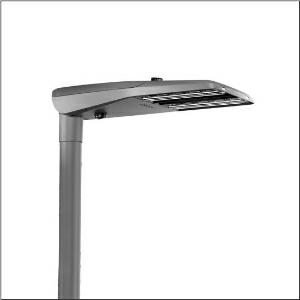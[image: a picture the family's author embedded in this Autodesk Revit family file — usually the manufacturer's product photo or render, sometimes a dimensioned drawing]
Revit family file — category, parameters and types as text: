
# Revit family: streetlight_sl_11_iq_midi___st1_2a_5xc3a21y08me_d9a7
name_source: partatom
category: Lighting Fixtures
units: mm (PartAtom-declared; Revit-internal decimal feet)

## family parameters
Cut with Voids When Loaded = No
Host = Face
Light Source = No
Part Type = Normal
Room Calculation Point = No
Round Connector Dimension = Use Diameter
Shared = No

## types (1)
- --- (1 x LED, 14840 lm, 122.8 W, 2200K)
    Apparent Load = 123 VA
    CIE Flux Codes = 32 70 96 100 100
    Color Rendering = 70
    Color Temperature = 2200K
    Default Elevation = 1800 mm
    Description = Streetlight SL 11 iQ midi, mast luminaire, primary light control with 3 zone facetted reflector, of plastic, silver coated, highly specular, primary optical cover: cover, of PMMA, transparent, light distribution: ST1.2a, light emission: direct distribution, primary light characteristic: asymmetric, installation type: post-top, side-entry, lamps: LED, High Power LED, rated values: 14.840lm | 122,8W | 120,8lm/W (begin service life); end service life: 14.840lm | 130,2W; at 50% lumin. flux: 7.420lm | 56,1W | 132,3lm/W, colour temperature: 2200K, colour rendering: CRI > 70, light colour: 722, light setting 1 begin service life: 100% | 14.840lm | 122,8W | 120,8lm/W | 2.200K, light setting 1 end service life: 130,2W, further light settings possible, control: pre-setting: logarithmic dimming characteristic, Street-Remote, Auto-Match, Temp-Guard, Lumen-Switch, Night-Set, Smart-Wire, Light-Fading, Desk-Remote (wireless, voltage-free reading and setting of iQ features in the workshop via application-optimized NFC function/RFID function), optimised constant luminous flux control (CLO 2.0), with cable H07RN-F 5x 1.5mm², mains connection: 230..240V, AC, 50/60Hz, connection cable pre-assembled, cable length: 12,5m, luminaire housing, of diecast aluminium, powder-coated, Siteco® metallic grey (DB 702S), please order mast flange separately, inclination adjustable without tools: 0°, 5°, 10°, 15° (post-top) | 0°, -5°, -10°, -15° (side-entry), sealing non-destructively replaceable, multi-level sealing system, length: 780mm, width: 376mm, height: 118mm, mast flange for spigot size: 42mm (side-entry): 5XC10008XM4, 60/48mm (side-entry/post-top): 5XC10108XM2, 76/60mm (side-entry/post-top): 5XC10108XM1, equipment: Power, Smart Interface below and above, protection rating (complete): IP66, insulation class (complete): insulation class II (safety insulation), certification: CE, ENEC, ENEC+, VDE, UKCA, impact resistance: IK10, permissible operating ambient temperature for outdoor applications: -25..+50°C, standard-compliant lighting for roads and squares, Environmental Product Declaration (EPD) tested and certified by an independent institute, packaging unit: 1 piece

Light Distribution: ST1.2a
    Height = 118 mm
    Lamp = 1 x LED
    Lamp Light Flux = 14840 lm
    Lamp Power = 122.8 W
    Lamp count = 1
    Length = 780 mm
    Luminous efficacy = 121 lm/W
    Manufacturer = Siteco
    ModVariant = No
    Model = 5XC3A21Y08ME
    Number of Poles = 1
    OnlyDefault = Yes
    Power Factor = 1
    Product Name = Streetlight SL 11 iQ midi | ST1.2a
    Product group = mast luminaire | pylon top
    ProductGroupID = 6100
    Protection Class = Protection class II
    Protection Degree = IP 66
    RLX_Detail_Level = 1
    RLX_Emergency_Light_Flux = 0 lm
    RLX_Emergency_Type = 0
    RLX_Emergency_Type_DB = No
    RlxData = <blob elided: 69765 chars, md5=d141115b>
    Socket = socket
    Standby Power = 0 W
    System Light Flux = 14840 lm
    System Power = 123 W
    Type Comments = factory setting: luminous flux: 100 % | dim-lin: 254 | 553 mA
    Type Image = l_1004429.jpg
    URL = http://relux.com
    VarID = @adj_150911
    Voltage = 0 V
    Weight = 0.00 kg
    Width = 376 mm

## geometry (parser evidence)
native form markers: Blend x4, Sweep x9
no freeform markers — native parametric forms only
